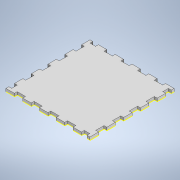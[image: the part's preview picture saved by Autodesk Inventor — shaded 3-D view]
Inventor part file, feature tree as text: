
AUTODESK INVENTOR PART (.ipt)
format: ipt  version: 2021 (Build 250183000, 183)  size: 372,224 bytes
history: native  units: mm
features: sketch x5, extrude x4, projected_geometry x2, pattern_linear x1, pattern_circular x1
ambient origin geometry x8: Origin, YZ Plane, XZ Plane, XY Plane, X Axis, Y Axis, Z Axis, Center Point
bodies: Solid1 (feature_tree)
feature tree (13):
  extrude  "Extrusion1"  Depth=120.0mm
  extrude  "Extrusion2"  Depth=60.0mm
  pattern_linear  "Rectangular Pattern1"  Spacing1=0.0mm  [1 undecoded]
  extrude  "Extrusion3"  Depth=12.0mm
  pattern_circular  "Circular Pattern3"  [2 undecoded]
  extrude  "Extrusion4"  Depth=24.0mm
  sketch  "Sketch5"  dims[d9=4.0mm d10=0.0mm d11=12.0mm d12=4.0mm d13=0.0mm d17=50.0mm d19=24.0mm d23=4.0mm d24=4.0mm d25=0.0mm d26=0.0mm d27=4.0mm d28=0.0mm d29=40.0mm d30=360.0deg d32=0.11mm d33=4.0mm d34=0.0mm]
  sketch  "Sketch1"  dims[d2=120.0mm d3=120.0mm]
  sketch  "Sketch2"  dims[d4=60.0mm d5=60.0mm]
  sketch  "Sketch3"  dims[d6=4.0mm d7=0.0mm]
  sketch  "Sketch4"  dims[d8=12.0mm]
  projected_geometry  "Projected Loop1"
  projected_geometry  "Projected Loop2"
note: 3 required parameter values undecoded (feature->parameter linkage not recoverable at this tier; creation-order binding heuristic only, values carry confidence <= 0.55)
